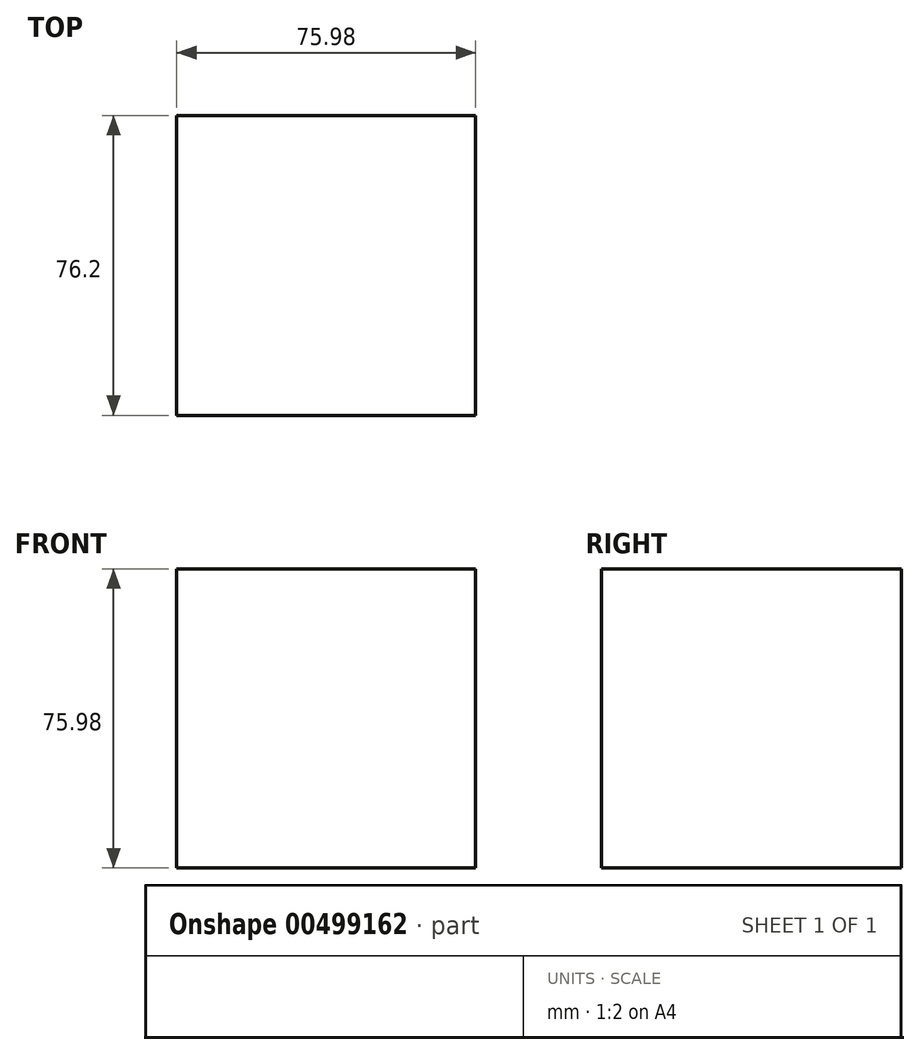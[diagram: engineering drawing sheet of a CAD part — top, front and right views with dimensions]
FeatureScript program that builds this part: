
annotation { "Feature Type Name" : "Feature", "Feature Type Description" : "" }
export const myFeature = defineFeature(function(context is Context, id is Id, definition is map)
    precondition{}
    {
        {
            var Q0;
            Q0=qCreatedBy(makeId("Front.planeOp"),FACE);
            var sketch = newSketch(context, id + "F0", { "sketchPlane" : qUnion([Q0])});
            skPoint(sketch, "E0.middle", {"position": v(0, 0) * mm});
            skLineSegment(sketch, "E1.bottom", {"start": v(0, 0) * mm, "end": v(-75.98, 0) * mm});
            skLineSegment(sketch, "E1.top", {"start": v(0, 75.98) * mm, "end": v(-75.98, 75.98) * mm});
            skLineSegment(sketch, "E1.left", {"start": v(0, 0) * mm, "end": v(0, 75.98) * mm});
            skLineSegment(sketch, "E1.right", {"start": v(-75.98, 0) * mm, "end": v(-75.98, 75.98) * mm});
            skSolve(sketch);
        }
        {
            var Q0;
            Q0=makeQuery(id+"F0.imprint","IMPRINT",FACE,{"disambiguationData":[TD([[makeQuery(id+"F0.imprint","IMPRINT",EDGE,{"derivedFrom":sQuery(id+"F0.wireOp",EDGE,"E1.bottom")}),-1.0]])]});
            extrude(context, id + "F1", {"entities" : qUnion([Q0]), "depth" : 76.2 * mm});
        }
    });
